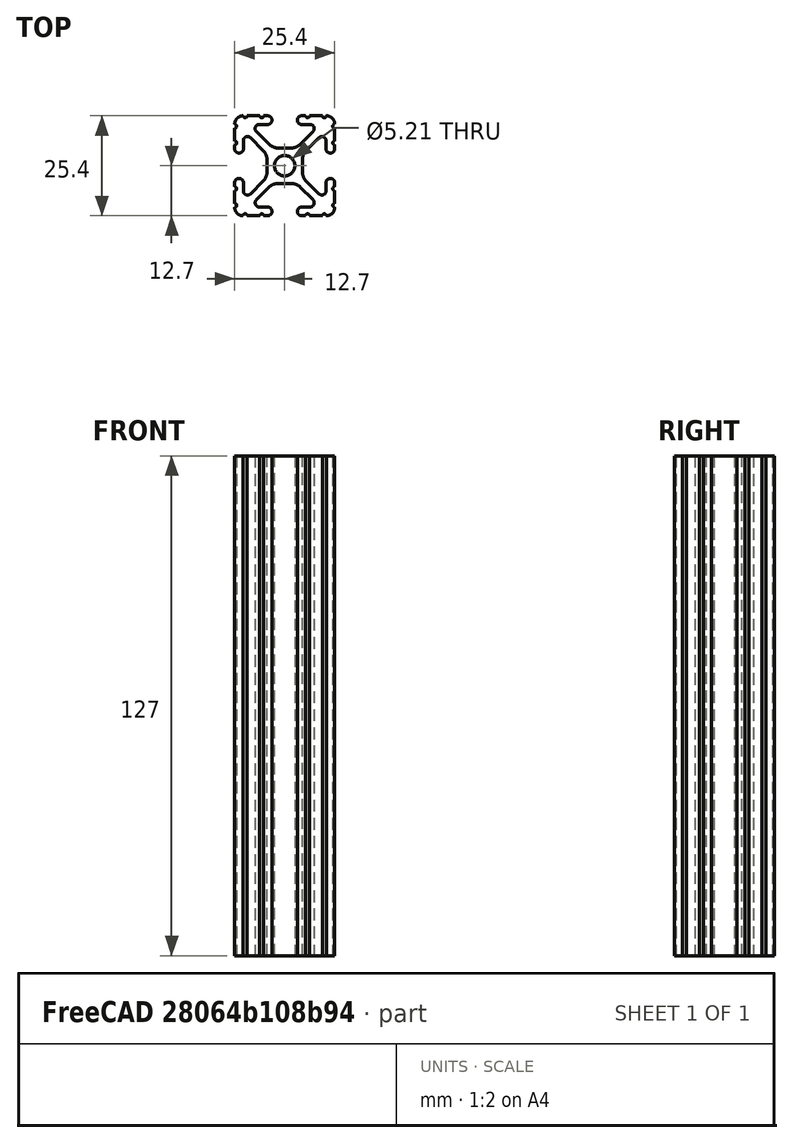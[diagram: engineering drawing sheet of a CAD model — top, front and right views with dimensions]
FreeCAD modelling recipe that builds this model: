
FCSTD DOCUMENT  (FreeCAD 0.19R24267 (Git))
Label: 1010-5
License: All rights reserved
LicenseURL: http://en.wikipedia.org/wiki/All_rights_reserved
objects: Sketcher::SketchObject×1, Part::Extrusion×1
note: 2 computed .brp shape members not serialized (recipe doc carries the construction recipe); baked Part::Feature solids carry a one-line shape summary decoded from their .brp

FEATURE [Sketcher::SketchObject] Sketch097
  FullyConstrained = false
  sketch-geometry (97):
    g0: Circle CenterX=0 CenterY=0 CenterZ=0 NormalX=0 NormalY=0 NormalZ=-1 AngleXU=0 Radius=2.6035
    g1: ArcOfCircle CenterX=12.7 CenterY=5.82508 CenterZ=0 NormalX=0 NormalY=0 NormalZ=1 AngleXU=0 Radius=0.508 StartAngle=1.5708 EndAngle=4.71239
    g2: LineSegment StartX=3.2385 StartY=11.651 StartZ=0 EndX=3.2385 EndY=11.5392 EndZ=0
    g3: LineSegment StartX=6.33313 StartY=-12.7 StartZ=0 EndX=9.55044 EndY=-12.7 EndZ=0
    g4: LineSegment StartX=7.20704 StartY=8.72437 StartZ=0 EndX=3.89827 EndY=5.42317 EndZ=0
    g5: ArcOfCircle CenterX=7.6835 CenterY=1.59319 CenterZ=0 NormalX=0 NormalY=0 NormalZ=1 AngleXU=0 Radius=3.175 StartAngle=2.35505 EndAngle=3.14159
    g6: ArcOfCircle CenterX=-1.70925 CenterY=-7.6708 CenterZ=0 NormalX=0 NormalY=0 NormalZ=1 AngleXU=0 Radius=3.175 StartAngle=1.5708 EndAngle=2.35528
    g7: ArcOfCircle CenterX=11.5392 CenterY=-4.28747 CenterZ=0 NormalX=0 NormalY=0 NormalZ=1 AngleXU=0 Radius=1.04901 StartAngle=1.5708 EndAngle=3.14159
    g8: ArcOfCircle CenterX=12.7 CenterY=-5.82508 CenterZ=0 NormalX=0 NormalY=0 NormalZ=1 AngleXU=0 Radius=0.508 StartAngle=1.5708 EndAngle=4.71239
    g9: LineSegment StartX=4.28751 StartY=10.4902 StartZ=0 EndX=6.47679 EndY=10.4902 EndZ=0
    g10: ArcOfCircle CenterX=4.28751 CenterY=11.651 CenterZ=0 NormalX=0 NormalY=0 NormalZ=1 AngleXU=0 Radius=1.04901 StartAngle=1.5708 EndAngle=3.14159
    g11: ArcOfCircle CenterX=6.47679 CenterY=9.45629 CenterZ=0 NormalX=0 NormalY=0 NormalZ=1 AngleXU=0 Radius=1.03391 StartAngle=5.49664 EndAngle=7.85398
    g12: ArcOfCircle CenterX=4.28751 CenterY=11.5392 CenterZ=0 NormalX=0 NormalY=0 NormalZ=1 AngleXU=0 Radius=1.04901 StartAngle=3.14159 EndAngle=4.71239
    g13: LineSegment StartX=3.95227 StartY=-5.42369 StartZ=0 EndX=7.17965 EndY=-8.64519 EndZ=0
    g14: ArcOfCircle CenterX=11.651 CenterY=4.28747 CenterZ=0 NormalX=0 NormalY=0 NormalZ=1 AngleXU=0 Radius=1.04901 StartAngle=4.71239 EndAngle=6.28319
    g15: ArcOfCircle CenterX=-5.82513 CenterY=-12.7 CenterZ=0 NormalX=0 NormalY=0 NormalZ=1 AngleXU=0 Radius=0.508 StartAngle=0 EndAngle=3.14159
    g16: LineSegment StartX=-6.47679 StartY=10.4902 StartZ=0 EndX=-4.28751 EndY=10.4902 EndZ=0
    g17: ArcOfCircle CenterX=-12.7 CenterY=10.0584 CenterZ=0 NormalX=0 NormalY=0 NormalZ=1 AngleXU=0 Radius=0.508 StartAngle=4.71239 EndAngle=7.85368
    g18: ArcOfCircle CenterX=-12.7 CenterY=5.82508 CenterZ=0 NormalX=0 NormalY=0 NormalZ=1 AngleXU=0 Radius=0.508 StartAngle=4.71239 EndAngle=7.85398
    g19: LineSegment StartX=-11.5392 StartY=-3.23846 StartZ=0 EndX=-11.651 EndY=-3.23846 EndZ=0
    g20: LineSegment StartX=-3.89827 StartY=5.42317 StartZ=0 EndX=-7.20704 EndY=8.72437 EndZ=0
    g21: LineSegment StartX=1.65578 StartY=4.4958 StartZ=0 EndX=-1.65578 EndY=4.4958 EndZ=0
    g22: ArcOfCircle CenterX=-1.65578 CenterY=7.6708 CenterZ=0 NormalX=0 NormalY=0 NormalZ=1 AngleXU=0 Radius=3.175 StartAngle=3.92813 EndAngle=4.71239
    g23: LineSegment StartX=-9.55044 StartY=-12.7 StartZ=0 EndX=-6.33313 EndY=-12.7 EndZ=0
    g24: ArcOfCircle CenterX=-5.82513 CenterY=12.7 CenterZ=0 NormalX=0 NormalY=0 NormalZ=1 AngleXU=0 Radius=0.508 StartAngle=3.14159 EndAngle=6.28319
    g25: ArcOfCircle CenterX=-4.28751 CenterY=11.651 CenterZ=0 NormalX=0 NormalY=0 NormalZ=1 AngleXU=0 Radius=1.04901 StartAngle=0 EndAngle=1.5708
    g26: LineSegment StartX=-12.7 StartY=-4.28747 StartZ=0 EndX=-12.7 EndY=-5.31708 EndZ=0
    g27: ArcOfCircle CenterX=-6.47679 CenterY=9.45629 CenterZ=0 NormalX=0 NormalY=0 NormalZ=1 AngleXU=0 Radius=1.03391 StartAngle=1.5708 EndAngle=3.92813
    g28: ArcOfCircle CenterX=-4.28751 CenterY=11.5392 CenterZ=0 NormalX=0 NormalY=0 NormalZ=1 AngleXU=0 Radius=1.04901 StartAngle=4.71239 EndAngle=6.28319
    g29: LineSegment StartX=-5.44101 StartY=-3.84082 StartZ=0 EndX=-8.73713 EndY=-7.12941 EndZ=0
    g30: ArcOfCircle CenterX=-7.6835 CenterY=-1.59319 CenterZ=0 NormalX=0 NormalY=0 NormalZ=1 AngleXU=0 Radius=3.175 StartAngle=5.49664 EndAngle=6.28319
    g31: LineSegment StartX=-12.7 StartY=5.31708 StartZ=0 EndX=-12.7 EndY=4.28747 EndZ=0
    g32: LineSegment StartX=-8.73713 StartY=7.12941 StartZ=0 EndX=-5.44101 EndY=3.84082 EndZ=0
    g33: LineSegment StartX=-11.651 StartY=3.23846 StartZ=0 EndX=-11.5392 EndY=3.23846 EndZ=0
    g34: ArcOfCircle CenterX=-9.46279 CenterY=-6.40209 CenterZ=0 NormalX=0 NormalY=0 NormalZ=1 AngleXU=0 Radius=1.02741 StartAngle=3.14159 EndAngle=5.49664
    g35: ArcOfCircle CenterX=-10.5918 CenterY=10.5918 CenterZ=0 NormalX=0 NormalY=0 NormalZ=1 AngleXU=0 Radius=2.1082 StartAngle=1.55877 EndAngle=3.15364
    g36: LineSegment StartX=-12.7 StartY=9.5504 StartZ=0 EndX=-12.7 EndY=6.33308 EndZ=0
    g37: LineSegment StartX=-6.33313 StartY=12.7 StartZ=0 EndX=-9.55044 EndY=12.7 EndZ=0
    g38: ArcOfCircle CenterX=-11.5392 CenterY=-4.28747 CenterZ=0 NormalX=0 NormalY=0 NormalZ=1 AngleXU=0 Radius=1.04901 StartAngle=0 EndAngle=1.5708
    g39: LineSegment StartX=4.28751 StartY=-12.7 StartZ=0 EndX=5.31713 EndY=-12.7 EndZ=0
    g40: LineSegment StartX=5.44101 StartY=3.84082 StartZ=0 EndX=8.73713 EndY=7.12941 EndZ=0
    g41: LineSegment StartX=10.4902 StartY=-4.28747 StartZ=0 EndX=10.4902 EndY=-6.40209 EndZ=0
    g42: ArcOfCircle CenterX=9.46279 CenterY=6.40209 CenterZ=0 NormalX=0 NormalY=0 NormalZ=1 AngleXU=0 Radius=1.02741 StartAngle=0 EndAngle=2.35505
    g43: ArcOfCircle CenterX=5.82513 CenterY=-12.7 CenterZ=0 NormalX=0 NormalY=0 NormalZ=1 AngleXU=0 Radius=0.508 StartAngle=0 EndAngle=3.14159
    g44: LineSegment StartX=12.7 StartY=-9.5504 StartZ=0 EndX=12.7 EndY=-6.33308 EndZ=0
    g45: LineSegment StartX=4.5085 StartY=-1.59319 StartZ=0 EndX=4.5085 EndY=1.59319 EndZ=0
    g46: ArcOfCircle CenterX=12.7 CenterY=10.0584 CenterZ=0 NormalX=0 NormalY=0 NormalZ=1 AngleXU=0 Radius=0.508 StartAngle=1.5711 EndAngle=4.71239
    g47: ArcOfCircle CenterX=12.7 CenterY=-10.0584 CenterZ=0 NormalX=0 NormalY=0 NormalZ=1 AngleXU=0 Radius=0.508 StartAngle=1.5708 EndAngle=4.71209
    g48: LineSegment StartX=3.2385 StartY=-11.5392 StartZ=0 EndX=3.2385 EndY=-11.651 EndZ=0
    g49: LineSegment StartX=8.73713 StartY=-7.12941 StartZ=0 EndX=5.44101 EndY=-3.84082 EndZ=0
    g50: ArcOfCircle CenterX=11.651 CenterY=-4.28747 CenterZ=0 NormalX=0 NormalY=0 NormalZ=1 AngleXU=0 Radius=1.04901 StartAngle=0 EndAngle=1.5708
    g51: ArcOfCircle CenterX=1.65578 CenterY=7.6708 CenterZ=0 NormalX=0 NormalY=0 NormalZ=1 AngleXU=0 Radius=3.175 StartAngle=4.71239 EndAngle=5.49664
    g52: ArcOfCircle CenterX=7.6835 CenterY=-1.59319 CenterZ=0 NormalX=0 NormalY=0 NormalZ=1 AngleXU=0 Radius=3.175 StartAngle=3.14159 EndAngle=3.92813
    g53: LineSegment StartX=12.7 StartY=4.28747 StartZ=0 EndX=12.7 EndY=5.31708 EndZ=0
    g54: ArcOfCircle CenterX=6.41641 CenterY=-9.40983 CenterZ=0 NormalX=0 NormalY=0 NormalZ=1 AngleXU=0 Radius=1.08037 StartAngle=4.71239 EndAngle=7.06949
    g55: LineSegment StartX=12.7 StartY=-5.31708 StartZ=0 EndX=12.7 EndY=-4.28747 EndZ=0
    g56: ArcOfCircle CenterX=10.0584 CenterY=-12.7 CenterZ=0 NormalX=0 NormalY=0 NormalZ=1 AngleXU=0 Radius=0.508 StartAngle=0.000300194 EndAngle=3.14159
    g57: ArcOfCircle CenterX=11.5392 CenterY=4.28747 CenterZ=0 NormalX=0 NormalY=0 NormalZ=1 AngleXU=0 Radius=1.04901 StartAngle=3.14159 EndAngle=4.71239
    g58: LineSegment StartX=12.7 StartY=6.33308 StartZ=0 EndX=12.7 EndY=9.5504 EndZ=0
    g59: ArcOfCircle CenterX=4.28751 CenterY=-11.5392 CenterZ=0 NormalX=0 NormalY=0 NormalZ=1 AngleXU=0 Radius=1.04901 StartAngle=1.5708 EndAngle=3.14159
    g60: ArcOfCircle CenterX=10.5918 CenterY=10.5918 CenterZ=0 NormalX=0 NormalY=0 NormalZ=1 AngleXU=0 Radius=2.1082 StartAngle=6.27114 EndAngle=7.86601
    g61: ArcOfCircle CenterX=9.46279 CenterY=-6.40209 CenterZ=0 NormalX=0 NormalY=0 NormalZ=1 AngleXU=0 Radius=1.02741 StartAngle=3.92813 EndAngle=6.28319
    g62: LineSegment StartX=6.41641 StartY=-10.4902 StartZ=0 EndX=4.28751 EndY=-10.4902 EndZ=0
    g63: LineSegment StartX=-10.4902 StartY=-6.40209 StartZ=0 EndX=-10.4902 EndY=-4.28747 EndZ=0
    g64: ArcOfCircle CenterX=-9.46279 CenterY=6.40209 CenterZ=0 NormalX=0 NormalY=0 NormalZ=1 AngleXU=0 Radius=1.02741 StartAngle=0.786542 EndAngle=3.14159
    g65: LineSegment StartX=-10.4902 StartY=4.28747 StartZ=0 EndX=-10.4902 EndY=6.40209 EndZ=0
    g66: LineSegment StartX=-4.5085 StartY=1.59319 StartZ=0 EndX=-4.5085 EndY=-1.59319 EndZ=0
    g67: LineSegment StartX=-4.28751 StartY=12.7 StartZ=0 EndX=-5.31713 EndY=12.7 EndZ=0
    g68: ArcOfCircle CenterX=-11.5392 CenterY=4.28747 CenterZ=0 NormalX=0 NormalY=0 NormalZ=1 AngleXU=0 Radius=1.04901 StartAngle=4.71239 EndAngle=6.28319
    g69: LineSegment StartX=-3.2385 StartY=11.5392 StartZ=0 EndX=-3.2385 EndY=11.651 EndZ=0
    g70: ArcOfCircle CenterX=-11.651 CenterY=4.28747 CenterZ=0 NormalX=0 NormalY=0 NormalZ=1 AngleXU=0 Radius=1.04901 StartAngle=3.14159 EndAngle=4.71239
    g71: ArcOfCircle CenterX=-7.6835 CenterY=1.59319 CenterZ=0 NormalX=0 NormalY=0 NormalZ=1 AngleXU=0 Radius=3.175 StartAngle=0 EndAngle=0.786542
    g72: ArcOfCircle CenterX=-10.0584 CenterY=12.7 CenterZ=0 NormalX=0 NormalY=0 NormalZ=1 AngleXU=0 Radius=0.508 StartAngle=3.14189 EndAngle=6.28319
    g73: LineSegment StartX=-1.70925 StartY=-4.4958 StartZ=0 EndX=1.70925 EndY=-4.4958 EndZ=0
    g74: LineSegment StartX=11.651 StartY=-3.23846 StartZ=0 EndX=11.5392 EndY=-3.23846 EndZ=0
    g75: ArcOfCircle CenterX=-10.5918 CenterY=-10.5918 CenterZ=0 NormalX=0 NormalY=0 NormalZ=1 AngleXU=0 Radius=2.1082 StartAngle=3.12954 EndAngle=4.72442
    g76: ArcOfCircle CenterX=10.5918 CenterY=-10.5918 CenterZ=0 NormalX=0 NormalY=0 NormalZ=1 AngleXU=0 Radius=2.1082 StartAngle=4.70036 EndAngle=6.29523
    g77: ArcOfCircle CenterX=-12.7 CenterY=-5.82508 CenterZ=0 NormalX=0 NormalY=0 NormalZ=1 AngleXU=0 Radius=0.508 StartAngle=4.71239 EndAngle=7.85398
    g78: ArcOfCircle CenterX=5.82513 CenterY=12.7 CenterZ=0 NormalX=0 NormalY=0 NormalZ=1 AngleXU=0 Radius=0.508 StartAngle=3.14159 EndAngle=6.28319
    g79: LineSegment StartX=9.55044 StartY=12.7 StartZ=0 EndX=6.33313 EndY=12.7 EndZ=0
    g80: ArcOfCircle CenterX=10.0584 CenterY=12.7 CenterZ=0 NormalX=0 NormalY=0 NormalZ=1 AngleXU=0 Radius=0.508 StartAngle=3.14159 EndAngle=6.28289
    g81: ArcOfCircle CenterX=1.70925 CenterY=-7.6708 CenterZ=0 NormalX=0 NormalY=0 NormalZ=1 AngleXU=0 Radius=3.175 StartAngle=0.78631 EndAngle=1.5708
    g82: ArcOfCircle CenterX=4.28751 CenterY=-11.651 CenterZ=0 NormalX=0 NormalY=0 NormalZ=1 AngleXU=0 Radius=1.04901 StartAngle=3.14159 EndAngle=4.71239
    g83: LineSegment StartX=5.31713 StartY=12.7 StartZ=0 EndX=4.28751 EndY=12.7 EndZ=0
    g84: LineSegment StartX=10.4902 StartY=6.40209 StartZ=0 EndX=10.4902 EndY=4.28747 EndZ=0
    g85: LineSegment StartX=11.5392 StartY=3.23846 StartZ=0 EndX=11.651 EndY=3.23846 EndZ=0
    g86: ArcOfCircle CenterX=-10.0584 CenterY=-12.7 CenterZ=0 NormalX=0 NormalY=0 NormalZ=1 AngleXU=0 Radius=0.508 StartAngle=0 EndAngle=3.14129
    g87: ArcOfCircle CenterX=-12.7 CenterY=-10.0584 CenterZ=0 NormalX=0 NormalY=0 NormalZ=1 AngleXU=0 Radius=0.508 StartAngle=4.71269 EndAngle=7.85398
    g88: ArcOfCircle CenterX=-4.28751 CenterY=-11.5392 CenterZ=0 NormalX=0 NormalY=0 NormalZ=1 AngleXU=0 Radius=1.04901 StartAngle=0 EndAngle=1.5708
    g89: ArcOfCircle CenterX=-4.28751 CenterY=-11.651 CenterZ=0 NormalX=0 NormalY=0 NormalZ=1 AngleXU=0 Radius=1.04901 StartAngle=4.71239 EndAngle=6.28319
    g90: LineSegment StartX=-12.7 StartY=-6.33308 StartZ=0 EndX=-12.7 EndY=-9.5504 EndZ=0
    g91: ArcOfCircle CenterX=-11.651 CenterY=-4.28747 CenterZ=0 NormalX=0 NormalY=0 NormalZ=1 AngleXU=0 Radius=1.04901 StartAngle=1.5708 EndAngle=3.14159
    g92: LineSegment StartX=-7.17965 StartY=-8.64519 StartZ=0 EndX=-3.95227 EndY=-5.42369 EndZ=0
    g93: LineSegment StartX=-5.31713 StartY=-12.7 StartZ=0 EndX=-4.28751 EndY=-12.7 EndZ=0
    g94: LineSegment StartX=-3.2385 StartY=-11.651 StartZ=0 EndX=-3.2385 EndY=-11.5392 EndZ=0
    g95: ArcOfCircle CenterX=-6.41641 CenterY=-9.40983 CenterZ=0 NormalX=0 NormalY=0 NormalZ=1 AngleXU=0 Radius=1.08037 StartAngle=2.35528 EndAngle=4.71239
    g96: LineSegment StartX=-4.28751 StartY=-10.4902 StartZ=0 EndX=-6.41641 EndY=-10.4902 EndZ=0
FEATURE [Part::Extrusion] Extrude
  Base = -> Sketch097
  Dir = (0,0,1)
  DirMode = 2
  FaceMakerClass = Part::FaceMakerBullseye
  LengthFwd = 127
  LengthRev = 0
  Solid = true
  Symmetric = false
